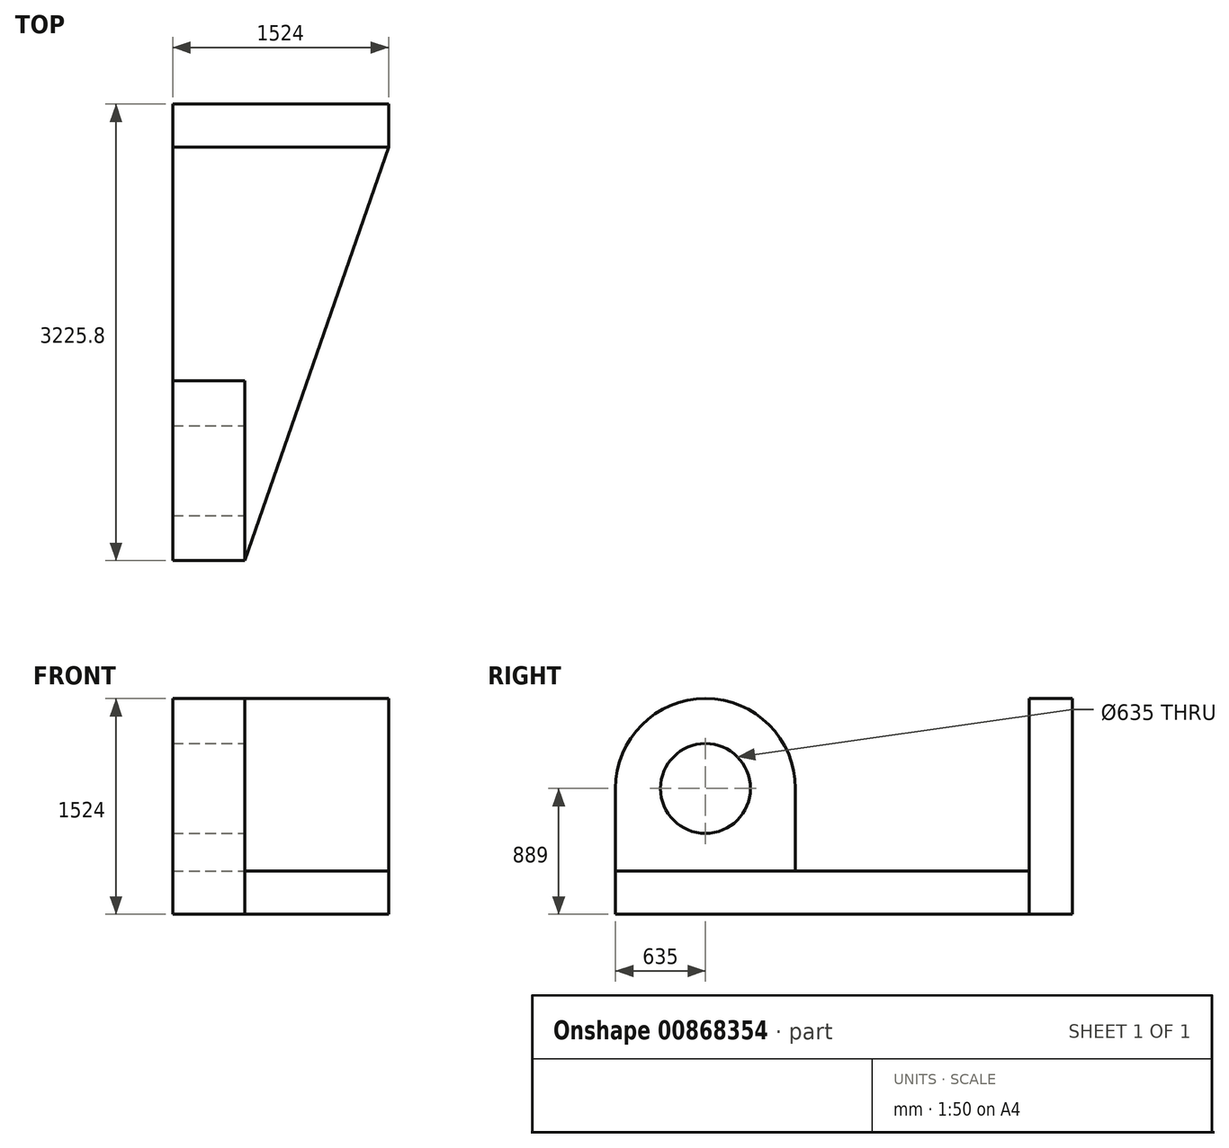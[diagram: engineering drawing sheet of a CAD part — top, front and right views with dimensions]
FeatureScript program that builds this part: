
annotation { "Feature Type Name" : "Feature", "Feature Type Description" : "" }
export const myFeature = defineFeature(function(context is Context, id is Id, definition is map)
    precondition{}
    {
        {
            var Q0;
            Q0=qCreatedBy(makeId("Front.planeOp"),FACE);
            var sketch = newSketch(context, id + "F0", { "sketchPlane" : qUnion([Q0])});
            skLineSegment(sketch, "E0.bottom", {"start": v(0, 0) * mm, "end": v(-1524, 0) * mm});
            skLineSegment(sketch, "E0.top", {"start": v(0, 1524) * mm, "end": v(-1524, 1524) * mm});
            skLineSegment(sketch, "E0.left", {"start": v(0, 0) * mm, "end": v(0, 1524) * mm});
            skLineSegment(sketch, "E0.right", {"start": v(-1524, 0) * mm, "end": v(-1524, 1524) * mm});
            skLineSegment(sketch, "E1.bottom", {"start": v(-415.26, -345.85) * mm, "end": v(-374.39, -345.85) * mm});
            skLineSegment(sketch, "E1.top", {"start": v(-415.26, -351.96) * mm, "end": v(-374.39, -351.96) * mm});
            skLineSegment(sketch, "E1.left", {"start": v(-415.26, -345.85) * mm, "end": v(-415.26, -351.96) * mm});
            skLineSegment(sketch, "E1.right", {"start": v(-374.39, -345.85) * mm, "end": v(-374.39, -351.96) * mm});
            skSolve(sketch);
        }
        {
            var Q0;
            Q0 = qSketchRegion(id + "F0", true);
            extrude(context, id + "F1", {"entities" : qUnion([Q0]), "depth" : 304.8 * mm, "offsetDistance" : 25.4 * mm});
        }
        {
            var Q0;
            Q0=makeQuery(id+"F1.opExtrude","CAP_FACE",FACE,{"disambiguationData":[OSD([sQuery(id+"F0.wireOp",EDGE,"E0.bottom"),sQuery(id+"F0.wireOp",EDGE,"E0.top"),sQuery(id+"F0.wireOp",EDGE,"E0.left"),sQuery(id+"F0.wireOp",EDGE,"E0.right")])],"isStart":false});
            var sketch = newSketch(context, id + "F2", { "sketchPlane" : qUnion([Q0])});
            skSolve(sketch);
        }
        {
            var Q0;
            Q0=makeQuery(id+"F2.imprint","IMPRINT",FACE,{"disambiguationData":[TD([[makeQuery(id+"F2.imprint","IMPRINT",EDGE,{"derivedFrom":makeQuery(id+"F1.opExtrude","CAP_EDGE",EDGE,{"disambiguationData":[OSD([sQuery(id+"F0.wireOp",EDGE,"E0.bottom")])],"isStart":false})}),-1.0]])]});
            var sketch = newSketch(context, id + "F3", { "sketchPlane" : qUnion([Q0])});
            skLineSegment(sketch, "E2.bottom", {"start": v(0, 0) * mm, "end": v(-1524, 0) * mm});
            skLineSegment(sketch, "E2.top", {"start": v(0, 304.8) * mm, "end": v(-1524, 304.8) * mm});
            skLineSegment(sketch, "E2.left", {"start": v(0, 0) * mm, "end": v(0, 304.8) * mm});
            skLineSegment(sketch, "E2.right", {"start": v(-1524, 0) * mm, "end": v(-1524, 304.8) * mm});
            skSolve(sketch);
        }
        {
            var Q0;
            Q0 = qSketchRegion(id + "F3", true);
            extrude(context, id + "F4", {"entities" : qUnion([Q0]), "operationType" : NewBodyOperationType.ADD, "depth" : 2921 * mm, "offsetDistance" : 25.4 * mm});
        }
        {
            var Q0;
            Q0=makeQuery(id+"F4.opExtrude","SWEPT_FACE",FACE,{"disambiguationData":[OSD([sQuery(id+"F3.wireOp",EDGE,"E2.top")])]});
            var sketch = newSketch(context, id + "F5", { "sketchPlane" : qUnion([Q0])});
            skLineSegment(sketch, "E3.bottom", {"start": v(-1524, -3225.8) * mm, "end": v(-1016, -3225.8) * mm});
            skLineSegment(sketch, "E3.top", {"start": v(-1524, -1955.8) * mm, "end": v(-1016, -1955.8) * mm});
            skLineSegment(sketch, "E3.left", {"start": v(-1524, -3225.8) * mm, "end": v(-1524, -1955.8) * mm});
            skLineSegment(sketch, "E3.right", {"start": v(-1016, -3225.8) * mm, "end": v(-1016, -1955.8) * mm});
            skSolve(sketch);
        }
        {
            var Q0;
            Q0=makeQuery(id+"F5.imprint","IMPRINT",FACE,{"disambiguationData":[TD([[makeQuery(id+"F5.imprint","IMPRINT",EDGE,{"derivedFrom":sQuery(id+"F5.wireOp",EDGE,"E3.bottom")}),-1.0]])]});
            extrude(context, id + "F6", {"entities" : qUnion([Q0]), "operationType" : NewBodyOperationType.ADD, "depth" : 584.2 * mm, "offsetDistance" : 25.4 * mm});
        }
        {
            var Q0;
            Q0=makeQuery(id+"F6.opExtrude","SWEPT_FACE",FACE,{"disambiguationData":[OSD([sQuery(id+"F5.wireOp",EDGE,"E3.right")])]});
            var sketch = newSketch(context, id + "F7", { "sketchPlane" : qUnion([Q0])});
            skCircle(sketch, "E4", {"center": v(-2590.8, 889) * mm, "radius": 635 * mm});
            skSolve(sketch);
        }
        {
            var Q0;
            {var subQ1=sQuery(id+"F5.wireOp",EDGE,"E3.right");var subQ2=makeQuery(id+"F6.opExtrude","CAP_EDGE",EDGE,{"disambiguationData":[OSD([subQ1])],"isStart":false});Q0=makeQuery(id+"F7.imprint","IMPRINT",FACE,{"disambiguationData":[TD([[makeQuery(id+"F7.imprint","IMPRINT",EDGE,{"derivedFrom":subQ2}),1.0]])]});}
            extrude(context, id + "F8", {"entities" : qUnion([Q0]), "operationType" : NewBodyOperationType.ADD, "oppositeDirection" : true, "depth" : 508 * mm, "offsetDistance" : 25.4 * mm});
        }
        {
            var Q0;
            {var subQ0=sQuery(id+"F5.wireOp",EDGE,"E3.right");Q0=makeQuery(id+"F8.boolean.opBoolean","MERGE",FACE,{"derivedFrom":[makeQuery(id+"F6.opExtrude","SWEPT_FACE",FACE,{"disambiguationData":[OSD([subQ0])]}),makeQuery(id+"F8.opExtrude","CAP_FACE",FACE,{"disambiguationData":[OSD([subQ0,sQuery(id+"F7.wireOp",EDGE,"E4")])],"isStart":true})]});}
            var sketch = newSketch(context, id + "F9", { "sketchPlane" : qUnion([Q0])});
            skCircle(sketch, "E5", {"center": v(-2590.8, 889) * mm, "radius": 317.5 * mm});
            skSolve(sketch);
        }
        {
            var Q0;
            Q0=makeQuery(id+"F9.imprint","IMPRINT",FACE,{"disambiguationData":[TD([[makeQuery(id+"F9.imprint","IMPRINT",EDGE,{"derivedFrom":sQuery(id+"F9.wireOp",EDGE,"E5")}),1.0]])]});
            extrude(context, id + "F10", {"entities" : qUnion([Q0]), "operationType" : NewBodyOperationType.REMOVE, "oppositeDirection" : true, "depth" : 2476.5 * mm, "offsetDistance" : 25.4 * mm});
        }
        {
            var Q0;
            Q0=makeQuery(id+"F4.opExtrude","SWEPT_FACE",FACE,{"disambiguationData":[OSD([sQuery(id+"F3.wireOp",EDGE,"E2.top")])]});
            var sketch = newSketch(context, id + "F11", { "sketchPlane" : qUnion([Q0])});
            skLineSegment(sketch, "E6", {"start": v(-1016, -3225.8) * mm, "end": v(0, -304.8) * mm});
            skLineSegment(sketch, "E7", {"start": v(0, -304.8) * mm, "end": v(0, -3225.8) * mm});
            skLineSegment(sketch, "E8", {"start": v(0, -3225.8) * mm, "end": v(-1016, -3225.8) * mm});
            skSolve(sketch);
        }
        {
            var Q0;
            Q0=makeQuery(id+"F11.imprint","IMPRINT",FACE,{"disambiguationData":[TD([[makeQuery(id+"F11.imprint","IMPRINT",EDGE,{"derivedFrom":sQuery(id+"F11.wireOp",EDGE,"E6")}),-1.0]])]});
            extrude(context, id + "F12", {"entities" : qUnion([Q0]), "operationType" : NewBodyOperationType.REMOVE, "oppositeDirection" : true, "depth" : 2288.54 * mm, "offsetDistance" : 25.4 * mm});
        }
        {
            var Q0;
            Q0=makeQuery(id+"F1.opExtrude","SWEPT_BODY",BODY,{"disambiguationData":[OSD([sQuery(id+"F0.wireOp",EDGE,"E1.bottom"),sQuery(id+"F0.wireOp",EDGE,"E1.top"),sQuery(id+"F0.wireOp",EDGE,"E1.left"),sQuery(id+"F0.wireOp",EDGE,"E1.right")])]});
            deleteBodies(context, id + "F13", {"entities" : qUnion([Q0])});
        }
    });
